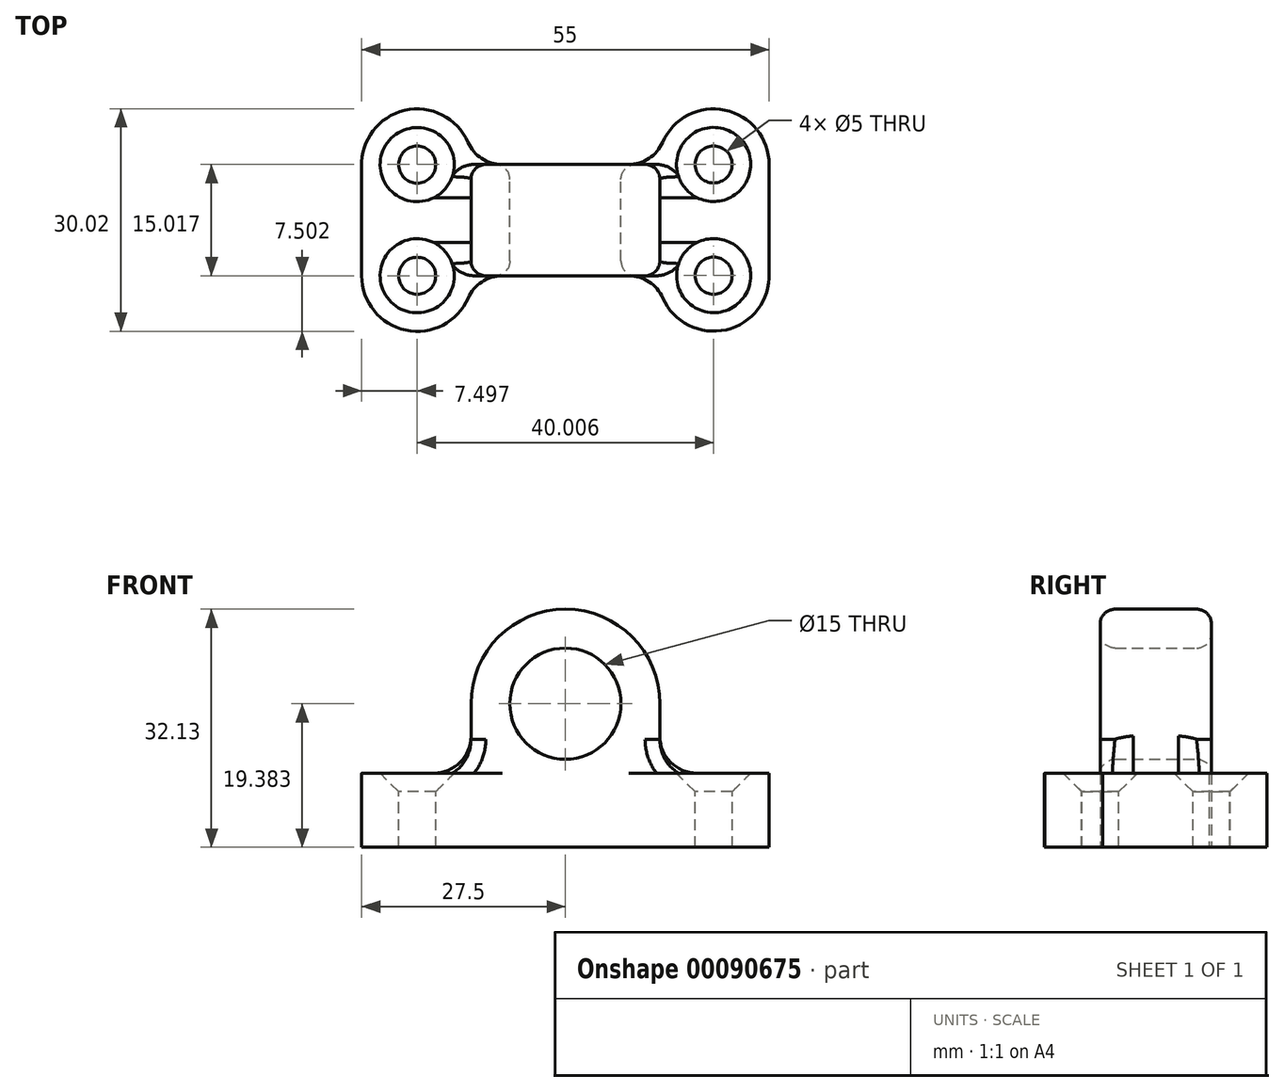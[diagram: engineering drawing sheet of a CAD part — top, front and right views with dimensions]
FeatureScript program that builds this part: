
annotation { "Feature Type Name" : "Feature", "Feature Type Description" : "" }
export const myFeature = defineFeature(function(context is Context, id is Id, definition is map)
    precondition{}
    {
        {
            var Q0;
            Q0=qCreatedBy(makeId("Top.planeOp"),FACE);
            var sketch = newSketch(context, id + "F0", { "sketchPlane" : qUnion([Q0])});
            skArc(sketch, "E0", {"start": v(-13.13, 10.5) * mm, "mid": v(-21.7, 14.8) * mm, "end": v(-27.5, 7.18) * mm});
            skLineSegment(sketch, "E1", {"start": v(0, 0) * mm, "end": v(-35.81, -0.02) * mm, "construction": true});
            skLineSegment(sketch, "E2", {"start": v(0, 0) * mm, "end": v(0, 22.8) * mm, "construction": true});
            skArc(sketch, "E3.MirrorC", {"start": v(12.5, 7.5) * mm, "mid": v(12.5, 7.5) * mm, "end": v(12.5, 7.5) * mm});
            skLineSegment(sketch, "E4.MirrorCS", {"start": v(0, 0) * mm, "end": v(35.81, 0.02) * mm, "construction": true});
            skArc(sketch, "E5.MirrorC", {"start": v(13.12, 10.5) * mm, "mid": v(21.53, 14.85) * mm, "end": v(27.5, 7.5) * mm});
            skArc(sketch, "E6.MirrorC", {"start": v(13.13, -10.5) * mm, "mid": v(21.7, -14.8) * mm, "end": v(27.5, -7.18) * mm});
            skArc(sketch, "E7.MirrorC", {"start": v(-13.12, -10.5) * mm, "mid": v(-21.53, -14.85) * mm, "end": v(-27.5, -7.5) * mm});
            skLineSegment(sketch, "E8.top", {"start": v(8.55, -7.5) * mm, "end": v(-8.54, -7.5) * mm});
            skLineSegment(sketch, "E8.left", {"start": v(27.5, 7.5) * mm, "end": v(27.5, -7.5) * mm});
            skLineSegment(sketch, "E8.right", {"start": v(-27.5, 7.5) * mm, "end": v(-27.5, -7.5) * mm});
            skPoint(sketch, "E8.middle", {"position": v(0, 0) * mm});
            skLineSegment(sketch, "E9.trimOffspring", {"start": v(8.54, 7.5) * mm, "end": v(-8.55, 7.5) * mm});
            skArc(sketch, "E10.filletArc", {"start": v(-13.13, 10.5) * mm, "mid": v(-11.29, 8.32) * mm, "end": v(-8.55, 7.5) * mm});
            skPoint(sketch, "E11.visualSharp", {"position": v(12.5, 7.5) * mm});
            skArc(sketch, "E11.filletArc", {"start": v(8.54, 7.5) * mm, "mid": v(11.28, 8.33) * mm, "end": v(13.12, 10.5) * mm});
            skPoint(sketch, "E12.visualSharp", {"position": v(-12.5, -7.5) * mm});
            skArc(sketch, "E12.filletArc", {"start": v(-8.54, -7.5) * mm, "mid": v(-11.28, -8.33) * mm, "end": v(-13.12, -10.5) * mm});
            skPoint(sketch, "E13.visualSharp", {"position": v(12.5, -7.5) * mm});
            skArc(sketch, "E13.filletArc", {"start": v(13.13, -10.5) * mm, "mid": v(11.29, -8.32) * mm, "end": v(8.55, -7.5) * mm});
            skSolve(sketch);
        }
        {
            var Q0;
            Q0 = qSketchRegion(id + "F0", true);
            extrude(context, id + "F1", {"entities" : qUnion([Q0]), "depth" : 10 * mm});
        }
        {
            var Q0;
            Q0=makeQuery(id+"F1.opExtrude","CAP_FACE",FACE,{"disambiguationData":[OSD([sQuery(id+"F0.wireOp",EDGE,"E0"),sQuery(id+"F0.wireOp",EDGE,"E6.MirrorC"),sQuery(id+"F0.wireOp",EDGE,"E7.MirrorC"),sQuery(id+"F0.wireOp",EDGE,"E8.top"),sQuery(id+"F0.wireOp",EDGE,"E8.left"),sQuery(id+"F0.wireOp",EDGE,"E8.right"),sQuery(id+"F0.wireOp",EDGE,"E9.trimOffspring"),sQuery(id+"F0.wireOp",EDGE,"E10.filletArc"),sQuery(id+"F0.wireOp",EDGE,"E11.filletArc"),sQuery(id+"F0.wireOp",EDGE,"E12.filletArc"),sQuery(id+"F0.wireOp",EDGE,"E13.filletArc"),sQuery(id+"F0.wireOp",EDGE,"E5.MirrorC")])],"isStart":false});
            var sketch = newSketch(context, id + "F2", { "sketchPlane" : qUnion([Q0])});
            skPoint(sketch, "E14", {"position": v(-20, 7.5) * mm});
            skPoint(sketch, "E15", {"position": v(-20, -7.5) * mm});
            skPoint(sketch, "E16", {"position": v(20, 7.5) * mm});
            skPoint(sketch, "E17", {"position": v(20, -7.5) * mm});
            skSolve(sketch);
        }
        {
            var Q0;
            Q0=sQuery(id+"F2.wireOp",VERTEX,"E14");
            var Q1;
            Q1=sQuery(id+"F2.wireOp",VERTEX,"E16");
            var Q2;
            Q2=sQuery(id+"F2.wireOp",VERTEX,"E17");
            var Q3;
            Q3=sQuery(id+"F2.wireOp",VERTEX,"E15");
            var Q4;
            Q4=makeQuery(id+"F1.opExtrude","SWEPT_BODY",BODY,{"disambiguationData":[OSD([sQuery(id+"F0.wireOp",EDGE,"E0"),sQuery(id+"F0.wireOp",EDGE,"E6.MirrorC"),sQuery(id+"F0.wireOp",EDGE,"E7.MirrorC"),sQuery(id+"F0.wireOp",EDGE,"E8.top"),sQuery(id+"F0.wireOp",EDGE,"E8.left"),sQuery(id+"F0.wireOp",EDGE,"E8.right"),sQuery(id+"F0.wireOp",EDGE,"E9.trimOffspring"),sQuery(id+"F0.wireOp",EDGE,"E10.filletArc"),sQuery(id+"F0.wireOp",EDGE,"E11.filletArc"),sQuery(id+"F0.wireOp",EDGE,"E12.filletArc"),sQuery(id+"F0.wireOp",EDGE,"E13.filletArc"),sQuery(id+"F0.wireOp",EDGE,"E5.MirrorC")])]});
            hole(context, id + "F3", {"style" : HoleStyle.C_SINK, "endStyle" : HoleEndStyle.THROUGH, "holeDiameter" : 5 * mm, "cSinkDiameter" : 10 * mm, "cSinkAngle" : 90 * degree, "locations" : qUnion([Q0, Q1, Q2, Q3]), "scope" : qUnion([Q4]), "isTappedThrough" : true});
        }
        {
            var Q0;
            Q0=qCreatedBy(makeId("Front.planeOp"),FACE);
            var sketch = newSketch(context, id + "F4", { "sketchPlane" : qUnion([Q0])});
            skLineSegment(sketch, "E18", {"start": v(0, 0) * mm, "end": v(0, 23.41) * mm, "construction": true});
            skCircle(sketch, "E19", {"center": v(0, 19.38) * mm, "radius": 7.5 * mm});
            skArc(sketch, "E20", {"start": v(-12.75, 19.38) * mm, "mid": v(0, 32.13) * mm, "end": v(12.75, 19.38) * mm});
            skLineSegment(sketch, "E21", {"start": v(-12.75, 19.38) * mm, "end": v(-12.75, 7.6) * mm});
            skLineSegment(sketch, "E22", {"start": v(-12.75, 7.6) * mm, "end": v(12.75, 7.6) * mm});
            skLineSegment(sketch, "E23", {"start": v(12.75, 7.6) * mm, "end": v(12.75, 19.38) * mm});
            skSolve(sketch);
        }
        {
            var Q0;
            Q0 = qSketchRegion(id + "F4", true);
            var Q1;
            Q1=makeQuery(id+"F1.opExtrude","SWEPT_FACE",FACE,{"disambiguationData":[OSD([sQuery(id+"F0.wireOp",EDGE,"E8.top")])]});
            var Q2;
            Q2=makeQuery(id+"F1.opExtrude","SWEPT_FACE",FACE,{"disambiguationData":[OSD([sQuery(id+"F0.wireOp",EDGE,"E9.trimOffspring")])]});
            extrude(context, id + "F5", {"entities" : qUnion([Q0]), "operationType" : NewBodyOperationType.ADD, "endBound" : BoundingType.UP_TO_SURFACE, "endBoundEntityFace" : qUnion([Q1]), "depth" : 25 * mm, "hasSecondDirection" : true, "secondDirectionBound" : SecondDirectionBoundingType.UP_TO_SURFACE, "secondDirectionOppositeDirection" : true, "secondDirectionBoundEntityFace" : qUnion([Q2]), "secondDirectionDepth" : 25 * mm});
        }
        {
            var Q0;
            Q0=makeQuery(id+"F5.boolean.opBoolean","INTERSECT",EDGE,{"derivedFrom":[makeQuery(id+"F1.opExtrude","CAP_FACE",FACE,{"disambiguationData":[OSD([sQuery(id+"F0.wireOp",EDGE,"E0"),sQuery(id+"F0.wireOp",EDGE,"E6.MirrorC"),sQuery(id+"F0.wireOp",EDGE,"E7.MirrorC"),sQuery(id+"F0.wireOp",EDGE,"E8.top"),sQuery(id+"F0.wireOp",EDGE,"E8.left"),sQuery(id+"F0.wireOp",EDGE,"E8.right"),sQuery(id+"F0.wireOp",EDGE,"E9.trimOffspring"),sQuery(id+"F0.wireOp",EDGE,"E10.filletArc"),sQuery(id+"F0.wireOp",EDGE,"E11.filletArc"),sQuery(id+"F0.wireOp",EDGE,"E12.filletArc"),sQuery(id+"F0.wireOp",EDGE,"E13.filletArc"),sQuery(id+"F0.wireOp",EDGE,"E5.MirrorC")])],"isStart":false}),makeQuery(id+"F5.opExtrude","SWEPT_FACE",FACE,{"disambiguationData":[OSD([sQuery(id+"F4.wireOp",EDGE,"E23")])]})]});
            var Q1;
            Q1=makeQuery(id+"F5.boolean.opBoolean","INTERSECT",EDGE,{"derivedFrom":[makeQuery(id+"F1.opExtrude","CAP_FACE",FACE,{"disambiguationData":[OSD([sQuery(id+"F0.wireOp",EDGE,"E0"),sQuery(id+"F0.wireOp",EDGE,"E6.MirrorC"),sQuery(id+"F0.wireOp",EDGE,"E7.MirrorC"),sQuery(id+"F0.wireOp",EDGE,"E8.top"),sQuery(id+"F0.wireOp",EDGE,"E8.left"),sQuery(id+"F0.wireOp",EDGE,"E8.right"),sQuery(id+"F0.wireOp",EDGE,"E9.trimOffspring"),sQuery(id+"F0.wireOp",EDGE,"E10.filletArc"),sQuery(id+"F0.wireOp",EDGE,"E11.filletArc"),sQuery(id+"F0.wireOp",EDGE,"E12.filletArc"),sQuery(id+"F0.wireOp",EDGE,"E13.filletArc"),sQuery(id+"F0.wireOp",EDGE,"E5.MirrorC")])],"isStart":false}),makeQuery(id+"F5.opExtrude","SWEPT_FACE",FACE,{"disambiguationData":[OSD([sQuery(id+"F4.wireOp",EDGE,"E21")])]})]});
            fillet(context, id + "F6", {"entities" : qUnion([Q0, Q1]), "radius" : 5 * mm, "tangentPropagation" : true, "allowEdgeOverflow" : false});
        }
        {
            var Q0;
            Q0=makeQuery(id+"F5.opExtrude","CAP_EDGE",EDGE,{"disambiguationData":[OSD([sQuery(id+"F4.wireOp",EDGE,"E19")])],"isStart":false});
            var Q1;
            Q1=makeQuery(id+"F5.opExtrude","CAP_EDGE",EDGE,{"disambiguationData":[OSD([sQuery(id+"F4.wireOp",EDGE,"E20")])],"isStart":false});
            var Q2;
            Q2=makeQuery(id+"F5.opExtrude","CAP_EDGE",EDGE,{"disambiguationData":[OSD([sQuery(id+"F4.wireOp",EDGE,"E20")])],"isStart":true});
            var Q3;
            Q3=makeQuery(id+"F5.opExtrude","CAP_EDGE",EDGE,{"disambiguationData":[OSD([sQuery(id+"F4.wireOp",EDGE,"E19")])],"isStart":true});
            fillet(context, id + "F7", {"entities" : qUnion([Q0, Q1, Q2, Q3]), "radius" : 2 * mm, "tangentPropagation" : true, "allowEdgeOverflow" : false});
        }
    });
